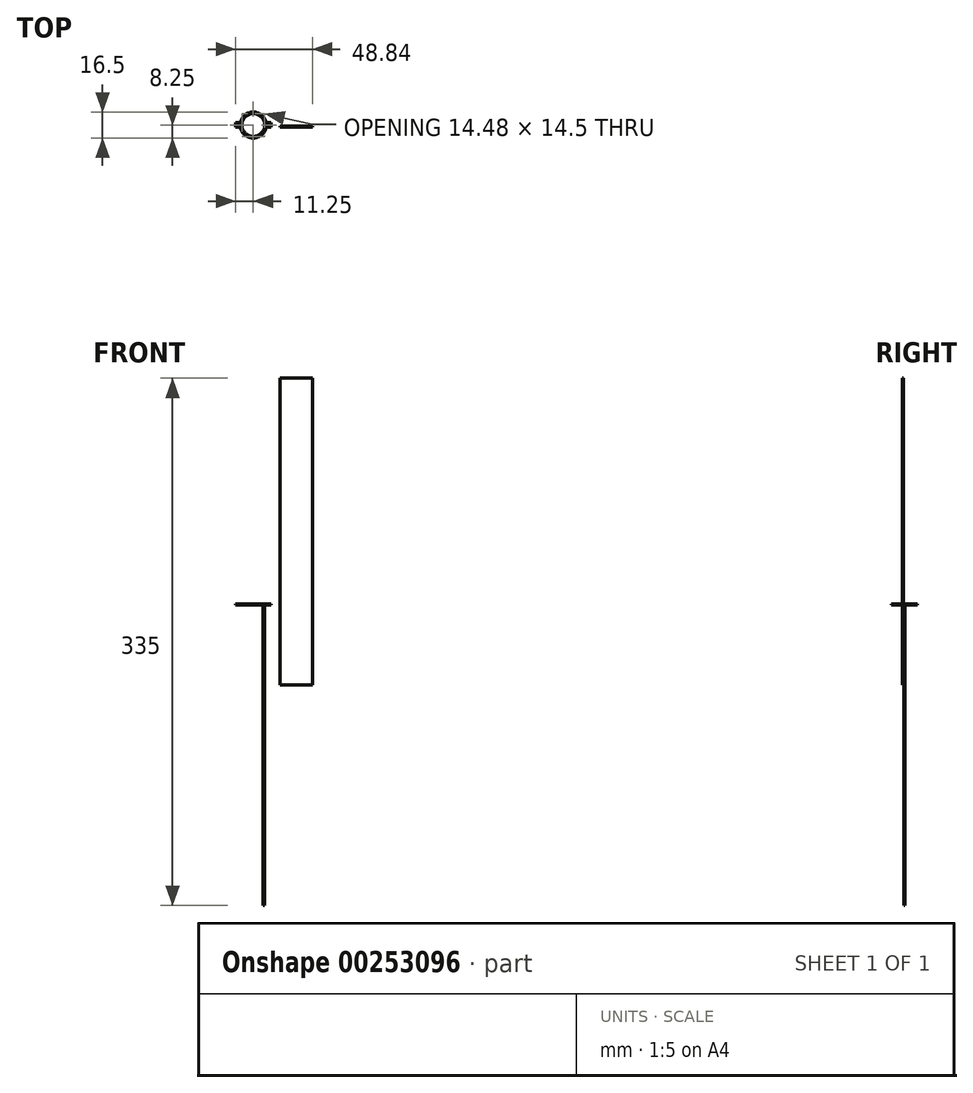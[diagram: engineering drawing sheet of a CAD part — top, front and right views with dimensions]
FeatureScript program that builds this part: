
annotation { "Feature Type Name" : "Feature", "Feature Type Description" : "" }
export const myFeature = defineFeature(function(context is Context, id is Id, definition is map)
    precondition{}
    {
        {
            var Q0;
            Q0=qCreatedBy(makeId("Top.planeOp"),FACE);
            var sketch = newSketch(context, id + "F0", { "sketchPlane" : qUnion([Q0])});
            skCircle(sketch, "E0", {"center": v(0, 0) * mm, "radius": 7.25 * mm});
            skLineSegment(sketch, "E1", {"start": v(7.24, 0.4) * mm, "end": v(10.25, 0.4) * mm});
            skLineSegment(sketch, "E2", {"start": v(10.25, 0.4) * mm, "end": v(10.25, -0.4) * mm});
            skLineSegment(sketch, "E3", {"start": v(10.25, -0.4) * mm, "end": v(7.24, -0.4) * mm});
            skLineSegment(sketch, "E4.MirrorCS", {"start": v(-10.25, 0.4) * mm, "end": v(-10.25, -0.4) * mm});
            skLineSegment(sketch, "E5.MirrorCS", {"start": v(-7.24, 0.4) * mm, "end": v(-10.25, 0.4) * mm});
            skLineSegment(sketch, "E6.MirrorCS", {"start": v(-10.25, -0.4) * mm, "end": v(-7.24, -0.4) * mm});
            skCircle(sketch, "E7.0", {"center": v(0, 0) * mm, "radius": 8.25 * mm});
            skLineSegment(sketch, "E8.0", {"start": v(11.25, 1.4) * mm, "end": v(11.25, -1.4) * mm});
            skLineSegment(sketch, "E9.0", {"start": v(8.13, 1.4) * mm, "end": v(11.25, 1.4) * mm});
            skLineSegment(sketch, "E10.0", {"start": v(11.25, -1.4) * mm, "end": v(8.13, -1.4) * mm});
            skLineSegment(sketch, "E11.MirrorCS", {"start": v(-8.13, 1.4) * mm, "end": v(-11.25, 1.4) * mm});
            skLineSegment(sketch, "E12.MirrorCS", {"start": v(-11.25, 1.4) * mm, "end": v(-11.25, -1.4) * mm});
            skLineSegment(sketch, "E13.MirrorCS", {"start": v(-11.25, -1.4) * mm, "end": v(-8.13, -1.4) * mm});
            skSolve(sketch);
        }
        {
            var Q0;
            {var subQ5=sQuery(id+"F0.wireOp",EDGE,"E4.MirrorCS");Q0=makeQuery(id+"F0.imprint","IMPRINT",FACE,{"disambiguationData":[TD([[makeQuery(id+"F0.imprint","IMPRINT",EDGE,{"derivedFrom":subQ5}),-1.0]])]});}
            var Q1;
            {var subQ4=sQuery(id+"F0.wireOp",EDGE,"E0");var subQ6=sQuery(id+"F0.wireOp",EDGE,"E1");var subQ7=makeQuery(id+"F0.imprint","INTERSECT",VERTEX,{"derivedFrom":[subQ6,subQ4]});Q1=makeQuery(id+"F0.imprint","IMPRINT",FACE,{"disambiguationData":[TD([[makeQuery(id+"F0.imprint","IMPRINT",EDGE,{"disambiguationData":[TD([[subQ7,-1.0]])],"derivedFrom":subQ6}),1.0]])]});}
            var Q2;
            {var subQ2=sQuery(id+"F0.wireOp",EDGE,"E3");var subQ5=sQuery(id+"F0.wireOp",EDGE,"E0");var subQ8=makeQuery(id+"F0.imprint","INTERSECT",VERTEX,{"derivedFrom":[subQ2,subQ5]});Q2=makeQuery(id+"F0.imprint","IMPRINT",FACE,{"disambiguationData":[TD([[makeQuery(id+"F0.imprint","IMPRINT",EDGE,{"disambiguationData":[TD([[subQ8,1.0]])],"derivedFrom":subQ2}),1.0]])]});}
            var Q3;
            {var subQ5=sQuery(id+"F0.wireOp",EDGE,"E2");Q3=makeQuery(id+"F0.imprint","IMPRINT",FACE,{"disambiguationData":[TD([[makeQuery(id+"F0.imprint","IMPRINT",EDGE,{"derivedFrom":subQ5}),1.0]])]});}
            extrude(context, id + "F1", {"entities" : qUnion([Q0, Q1, Q2, Q3]), "depth" : 50.5 * mm});
        }
        {
            var Q0;
            Q0=qCreatedBy(makeId("Top.planeOp"),FACE);
            var sketch = newSketch(context, id + "F2", { "sketchPlane" : qUnion([Q0])});
            skLineSegment(sketch, "E14.bottom", {"start": v(17.1, -0.62) * mm, "end": v(37.6, -0.62) * mm});
            skLineSegment(sketch, "E14.top", {"start": v(17.1, -1.37) * mm, "end": v(37.6, -1.37) * mm});
            skLineSegment(sketch, "E14.left", {"start": v(17.1, -0.62) * mm, "end": v(17.1, -1.37) * mm});
            skLineSegment(sketch, "E14.right", {"start": v(37.6, -0.62) * mm, "end": v(37.6, -1.37) * mm});
            skSolve(sketch);
        }
        {
            var Q0;
            Q0=makeQuery(id+"F2.imprint","IMPRINT",FACE,{"disambiguationData":[TD([[makeQuery(id+"F2.imprint","IMPRINT",EDGE,{"derivedFrom":sQuery(id+"F2.wireOp",EDGE,"E14.bottom")}),-1.0]])]});
            extrude(context, id + "F3", {"entities" : qUnion([Q0]), "depth" : 195 * mm});
        }
        {
            var Q0;
            Q0=makeQuery(id+"F1.opExtrude","CAP_FACE",FACE,{"disambiguationData":[OSD([sQuery(id+"F0.wireOp",EDGE,"E1"),sQuery(id+"F0.wireOp",EDGE,"E2"),sQuery(id+"F0.wireOp",EDGE,"E3"),sQuery(id+"F0.wireOp",EDGE,"E4.MirrorCS"),sQuery(id+"F0.wireOp",EDGE,"E0"),sQuery(id+"F0.wireOp",EDGE,"E5.MirrorCS"),sQuery(id+"F0.wireOp",EDGE,"E6.MirrorCS"),sQuery(id+"F0.wireOp",EDGE,"E7.0"),sQuery(id+"F0.wireOp",EDGE,"E8.0"),sQuery(id+"F0.wireOp",EDGE,"E9.0"),sQuery(id+"F0.wireOp",EDGE,"E10.0"),sQuery(id+"F0.wireOp",EDGE,"E11.MirrorCS"),sQuery(id+"F0.wireOp",EDGE,"E12.MirrorCS"),sQuery(id+"F0.wireOp",EDGE,"E13.MirrorCS")])],"isStart":true});
            extrude(context, id + "F4", {"entities" : qUnion([Q0]), "operationType" : NewBodyOperationType.ADD, "depth" : 140 * mm});
        }
        {
            var Q0;
            Q0=makeQuery(id+"F1.opExtrude","CAP_FACE",FACE,{"disambiguationData":[OSD([sQuery(id+"F0.wireOp",EDGE,"E1"),sQuery(id+"F0.wireOp",EDGE,"E2"),sQuery(id+"F0.wireOp",EDGE,"E3"),sQuery(id+"F0.wireOp",EDGE,"E4.MirrorCS"),sQuery(id+"F0.wireOp",EDGE,"E0"),sQuery(id+"F0.wireOp",EDGE,"E5.MirrorCS"),sQuery(id+"F0.wireOp",EDGE,"E6.MirrorCS"),sQuery(id+"F0.wireOp",EDGE,"E7.0"),sQuery(id+"F0.wireOp",EDGE,"E8.0"),sQuery(id+"F0.wireOp",EDGE,"E9.0"),sQuery(id+"F0.wireOp",EDGE,"E10.0"),sQuery(id+"F0.wireOp",EDGE,"E11.MirrorCS"),sQuery(id+"F0.wireOp",EDGE,"E12.MirrorCS"),sQuery(id+"F0.wireOp",EDGE,"E13.MirrorCS")])],"isStart":false});
            extrude(context, id + "F5", {"entities" : qUnion([Q0]), "operationType" : NewBodyOperationType.ADD, "depth" : 1 * mm});
        }
        {
            var Q0;
            {var subQ0=sQuery(id+"F0.wireOp",EDGE,"E2");Q0=makeQuery(id+"F5.boolean.opBoolean","MERGE",FACE,{"derivedFrom":[makeQuery(id+"F4.boolean.opBoolean","MERGE",FACE,{"derivedFrom":[makeQuery(id+"F1.opExtrude","SWEPT_FACE",FACE,{"disambiguationData":[OSD([subQ0])]}),makeQuery(id+"F4.opExtrude","SWEPT_FACE",FACE,{"disambiguationData":[OSD([subQ0])]})]}),makeQuery(id+"F5.opExtrude","SWEPT_FACE",FACE,{"disambiguationData":[OSD([subQ0])]})]});}
            extrude(context, id + "F6", {"entities" : qUnion([Q0]), "operationType" : NewBodyOperationType.ADD, "depth" : 4 * mm});
        }
        {
            var Q0;
            {var subQ0=sQuery(id+"F0.wireOp",EDGE,"E4.MirrorCS");Q0=makeQuery(id+"F5.boolean.opBoolean","MERGE",FACE,{"derivedFrom":[makeQuery(id+"F4.boolean.opBoolean","MERGE",FACE,{"derivedFrom":[makeQuery(id+"F1.opExtrude","SWEPT_FACE",FACE,{"disambiguationData":[OSD([subQ0])]}),makeQuery(id+"F4.opExtrude","SWEPT_FACE",FACE,{"disambiguationData":[OSD([subQ0])]})]}),makeQuery(id+"F5.opExtrude","SWEPT_FACE",FACE,{"disambiguationData":[OSD([subQ0])]})]});}
            extrude(context, id + "F7", {"entities" : qUnion([Q0]), "operationType" : NewBodyOperationType.ADD, "depth" : 4 * mm});
        }
        {
            var Q0;
            {var subQ0=sQuery(id+"F0.wireOp",EDGE,"E4.MirrorCS");var subQ1=sQuery(id+"F0.wireOp",EDGE,"E2");Q0=makeQuery(id+"F7.boolean.opBoolean","MERGE",FACE,{"derivedFrom":[makeQuery(id+"F6.boolean.opBoolean","MERGE",FACE,{"derivedFrom":[makeQuery(id+"F4.opExtrude","CAP_FACE",FACE,{"disambiguationData":[OSD([sQuery(id+"F0.wireOp",EDGE,"E1"),subQ1,sQuery(id+"F0.wireOp",EDGE,"E3"),subQ0,sQuery(id+"F0.wireOp",EDGE,"E0"),sQuery(id+"F0.wireOp",EDGE,"E5.MirrorCS"),sQuery(id+"F0.wireOp",EDGE,"E6.MirrorCS"),sQuery(id+"F0.wireOp",EDGE,"E7.0"),sQuery(id+"F0.wireOp",EDGE,"E8.0"),sQuery(id+"F0.wireOp",EDGE,"E9.0"),sQuery(id+"F0.wireOp",EDGE,"E10.0"),sQuery(id+"F0.wireOp",EDGE,"E11.MirrorCS"),sQuery(id+"F0.wireOp",EDGE,"E12.MirrorCS"),sQuery(id+"F0.wireOp",EDGE,"E13.MirrorCS")])],"isStart":false}),makeQuery(id+"F6.opExtrude","SWEPT_FACE",FACE,{"disambiguationData":[OSD([subQ1]),TDD([makeQuery(id+"F4.opExtrude","CAP_EDGE",EDGE,{"disambiguationData":[OSD([subQ1])],"isStart":false})])]})]}),makeQuery(id+"F7.opExtrude","SWEPT_FACE",FACE,{"disambiguationData":[OSD([subQ0]),TDD([makeQuery(id+"F4.opExtrude","CAP_EDGE",EDGE,{"disambiguationData":[OSD([subQ0])],"isStart":false})])]})]});}
            var sketch = newSketch(context, id + "F8", { "sketchPlane" : qUnion([Q0])});
            skArc(sketch, "E15", {"start": v(-7.24, 0.4) * mm, "mid": v(-7.28, 0) * mm, "end": v(-7.24, -0.4) * mm});
            skLineSegment(sketch, "E16", {"start": v(0, 7.25) * mm, "end": v(0, -7.25) * mm});
            skArc(sketch, "E17.MirrorCS", {"start": v(7.24, 0.4) * mm, "mid": v(7.28, 0) * mm, "end": v(7.24, -0.4) * mm});
            skSolve(sketch);
        }
        {
            var Q0;
            Q0=makeQuery(id+"F8.imprint","IMPRINT",FACE,{"disambiguationData":[TD([[makeQuery(id+"F8.imprint","IMPRINT",EDGE,{"derivedFrom":sQuery(id+"F8.wireOp",EDGE,"E17.MirrorCS")}),-1.0]])]});
            var Q1;
            Q1=makeQuery(id+"F8.imprint","IMPRINT",FACE,{"disambiguationData":[TD([[makeQuery(id+"F8.imprint","IMPRINT",EDGE,{"derivedFrom":sQuery(id+"F8.wireOp",EDGE,"E15")}),1.0]])]});
            extrude(context, id + "F9", {"entities" : qUnion([Q0, Q1]), "operationType" : NewBodyOperationType.REMOVE, "oppositeDirection" : true, "depth" : 190.9 * mm});
        }
        {
            var Q0;
            {var subQ0=sQuery(id+"F0.wireOp",EDGE,"E4.MirrorCS");var subQ1=sQuery(id+"F0.wireOp",EDGE,"E2");Q0=makeQuery(id+"F7.boolean.opBoolean","MERGE",FACE,{"derivedFrom":[makeQuery(id+"F6.boolean.opBoolean","MERGE",FACE,{"derivedFrom":[makeQuery(id+"F4.opExtrude","CAP_FACE",FACE,{"disambiguationData":[OSD([sQuery(id+"F0.wireOp",EDGE,"E1"),subQ1,sQuery(id+"F0.wireOp",EDGE,"E3"),subQ0,sQuery(id+"F0.wireOp",EDGE,"E0"),sQuery(id+"F0.wireOp",EDGE,"E5.MirrorCS"),sQuery(id+"F0.wireOp",EDGE,"E6.MirrorCS"),sQuery(id+"F0.wireOp",EDGE,"E7.0"),sQuery(id+"F0.wireOp",EDGE,"E8.0"),sQuery(id+"F0.wireOp",EDGE,"E9.0"),sQuery(id+"F0.wireOp",EDGE,"E10.0"),sQuery(id+"F0.wireOp",EDGE,"E11.MirrorCS"),sQuery(id+"F0.wireOp",EDGE,"E12.MirrorCS"),sQuery(id+"F0.wireOp",EDGE,"E13.MirrorCS")])],"isStart":false}),makeQuery(id+"F6.opExtrude","SWEPT_FACE",FACE,{"disambiguationData":[OSD([subQ1]),TDD([makeQuery(id+"F4.opExtrude","CAP_EDGE",EDGE,{"disambiguationData":[OSD([subQ1])],"isStart":false})])]})]}),makeQuery(id+"F7.opExtrude","SWEPT_FACE",FACE,{"disambiguationData":[OSD([subQ0]),TDD([makeQuery(id+"F4.opExtrude","CAP_EDGE",EDGE,{"disambiguationData":[OSD([subQ0])],"isStart":false})])]})]});}
            var sketch = newSketch(context, id + "F10", { "sketchPlane" : qUnion([Q0])});
            skLineSegment(sketch, "E18", {"start": v(7.24, 0.4) * mm, "end": v(10.25, 0.4) * mm});
            skLineSegment(sketch, "E19", {"start": v(7.24, -0.4) * mm, "end": v(10.25, -0.4) * mm});
            skLineSegment(sketch, "E20", {"start": v(0, 8.25) * mm, "end": v(0, -8.25) * mm});
            skLineSegment(sketch, "E21.MirrorCS", {"start": v(-7.24, 0.4) * mm, "end": v(-10.25, 0.4) * mm});
            skLineSegment(sketch, "E22.MirrorCS", {"start": v(-7.24, -0.4) * mm, "end": v(-10.25, -0.4) * mm});
            skLineSegment(sketch, "E23", {"start": v(-10.25, 0.4) * mm, "end": v(-10.25, -0.4) * mm});
            skLineSegment(sketch, "E24.MirrorCS", {"start": v(10.25, 0.4) * mm, "end": v(10.25, -0.4) * mm});
            skArc(sketch, "E25.MirrorCS", {"start": v(7.24, 0.4) * mm, "mid": v(7.25, 0) * mm, "end": v(7.24, -0.4) * mm});
            skLineSegment(sketch, "E26", {"start": v(-7.24, 0.4) * mm, "end": v(-7.24, -0.4) * mm});
            skSolve(sketch);
        }
        {
            var Q0;
            Q0=makeQuery(id+"F10.imprint","IMPRINT",FACE,{"disambiguationData":[TD([[makeQuery(id+"F10.imprint","IMPRINT",EDGE,{"derivedFrom":sQuery(id+"F10.wireOp",EDGE,"E21.MirrorCS")}),1.0]])]});
            var Q1;
            Q1=makeQuery(id+"F10.imprint","IMPRINT",FACE,{"disambiguationData":[TD([[makeQuery(id+"F10.imprint","IMPRINT",EDGE,{"derivedFrom":sQuery(id+"F10.wireOp",EDGE,"E18")}),-1.0]])]});
            extrude(context, id + "F11", {"entities" : qUnion([Q0, Q1]), "operationType" : NewBodyOperationType.REMOVE, "oppositeDirection" : true, "depth" : 190.9 * mm});
        }
    });
